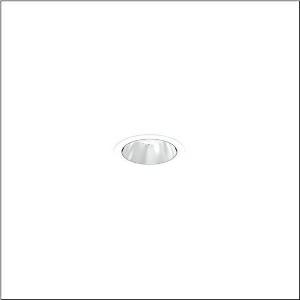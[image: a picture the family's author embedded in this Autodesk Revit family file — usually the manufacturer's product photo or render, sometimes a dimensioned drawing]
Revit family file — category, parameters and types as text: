
# Revit family: lunis_21_s_51db15ea91c
name_source: partatom
category: Lighting Fixtures
units: mm (PartAtom-declared; Revit-internal decimal feet)

## family parameters
Cut with Voids When Loaded = No
Host = Face
Light Source = No
Part Type = Normal
Room Calculation Point = No
Round Connector Dimension = Use Diameter
Shared = No

## types (1)
- --- (1 x LED, 1250 lm, 8 W, 6500K)
    Apparent Load = 8 VA
    CIE Flux Codes = 93 99 100 100 100
    Color Rendering = 80
    Color Temperature = 6500K
    Default Elevation = 1800 mm
    Description = Lunis 21,  S, downlight, light control with lens, of PMMA, anti glare with reflector, of PC, highly specular, light emission: direct distribution, LED rated luminous flux: 960lm, light colour: 830/840/865, with terminal, 5-pole, mains connection: 220..240V, AC, 50..60Hz, housing, round, of diecast aluminium, traffic white (RAL 9016), diameter: 84mm, clamping range: 1..40mm, protection rating (complete): IP20, protection rating (on room side): IP54, insulation class (complete): insulation class II (safety insulation), certification: CE, impact resistance: IK03, packaging unit: 1 piece
    Height = 0 mm  [stored 0 ft]
    Lamp = 1 x LED
    Lamp Light Flux = 1250 lm
    Lamp Power = 8 W
    Lamp count = 1
    Length = 84 mm
    Luminous efficacy = 156 lm/W
    Manufacturer = Siteco
    ModVariant = No
    Model = 51DB15EA91C
    Mounting Place = Ceiling
    Mounting Type = Recessed
    Number of Poles = 1
    OnlyDefault = Yes
    Power Factor = 1
    Product Name = Lunis 21 S
    Product group = downlight
    ProductGroupID = 400
    Protection Class = Protection class II
    Protection Degree = IP 20
    RLX_Detail_Level = 1
    RLX_Emergency_Light_Flux = 0 lm
    RLX_Emergency_Type = 0
    RLX_Emergency_Type_DB = No
    RlxData = <blob elided: 9381 chars, md5=612e380d>
    Socket = socket
    Standby Power = 0 W
    System Light Flux = 1250 lm
    System Power = 8 W
    Type Comments = individual setting: colour temperature 6500K, luminous flux: 100 % | (OFF | OFF | ON | OFF) | 200 mA
    Type Image = l_1290840.jpg
    URL = http://relux.com
    VarID = @adj_020732
    Voltage = 0 V
    Weight = 0.00 kg
    Width = 0 mm  [stored 0 ft]

note: [stored X ft] marks values corroborated as IEEE doubles in the binary element streams (Revit-internal decimal feet)

## geometry (parser evidence)
native form markers: Sweep x11
no freeform markers — native parametric forms only
